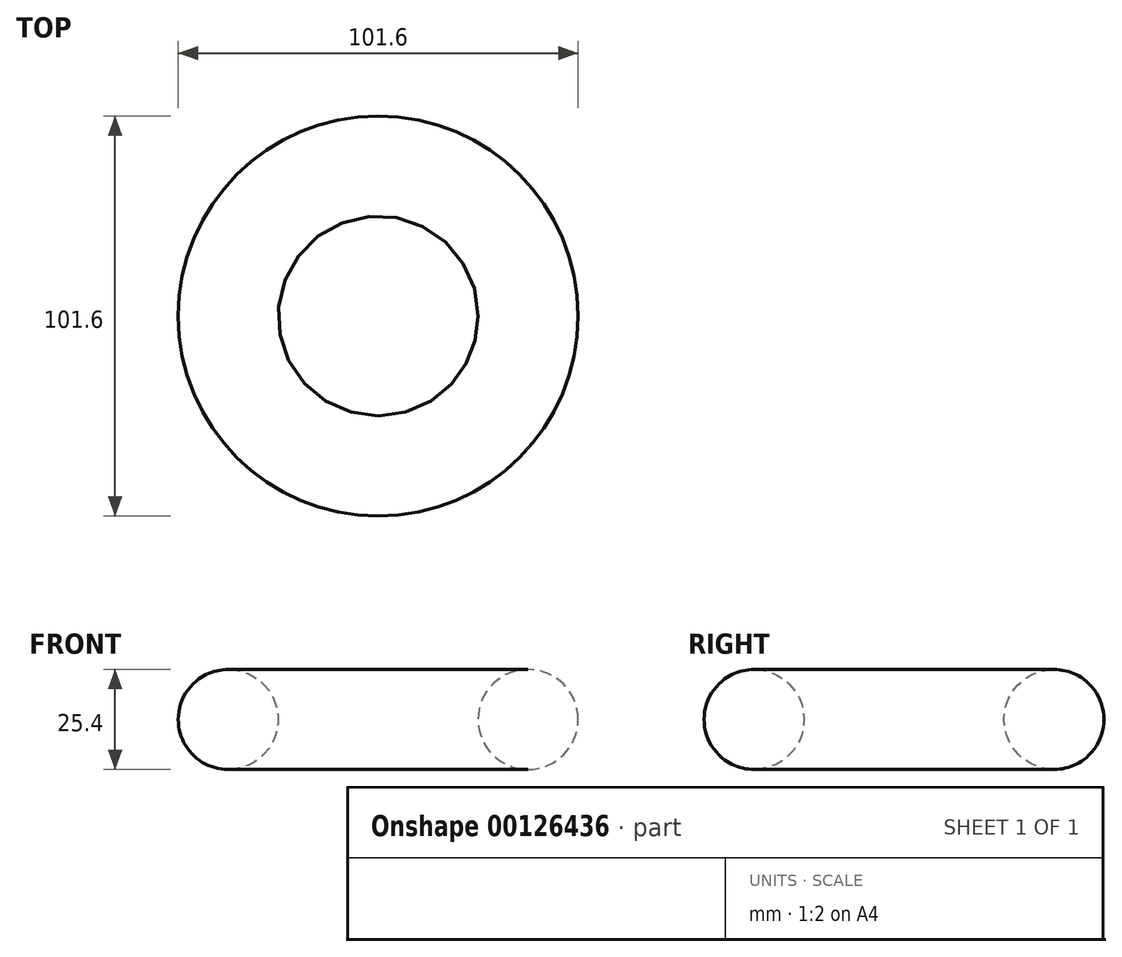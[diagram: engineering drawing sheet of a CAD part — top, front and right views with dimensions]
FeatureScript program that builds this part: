
annotation { "Feature Type Name" : "Feature", "Feature Type Description" : "" }
export const myFeature = defineFeature(function(context is Context, id is Id, definition is map)
    precondition{}
    {
        {
            var Q0;
            Q0=qCreatedBy(makeId("Front.planeOp"),FACE);
            var sketch = newSketch(context, id + "F0", { "sketchPlane" : qUnion([Q0])});
            skCircle(sketch, "E0", {"center": v(38.1, 0) * mm, "radius": 12.7 * mm});
            skLineSegment(sketch, "E1", {"start": v(0, 41.21) * mm, "end": v(0, -42.5) * mm, "construction": true});
            skSolve(sketch);
        }
        {
            var Q0;
            Q0 = qSketchRegion(id + "F0", true);
            var Q1;
            Q1=sQuery(id+"F0.wireOp",EDGE,"E1");
            revolve(context, id + "F1", {"entities" : qUnion([Q0]), "axis" : qUnion([Q1]), "revolveType" : RevolveType.FULL});
        }
    });
